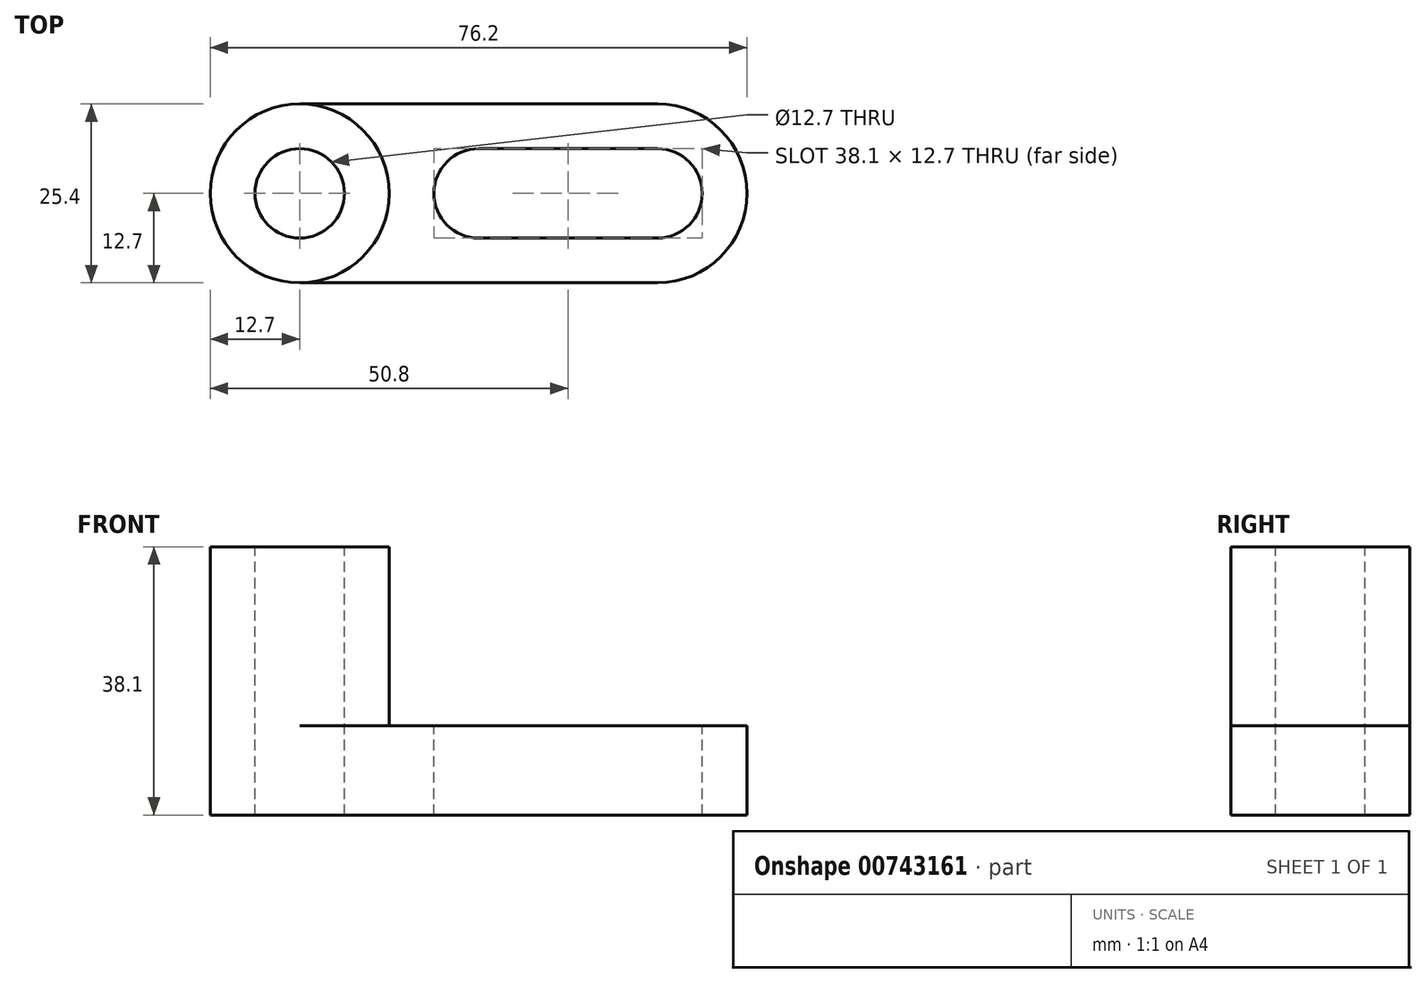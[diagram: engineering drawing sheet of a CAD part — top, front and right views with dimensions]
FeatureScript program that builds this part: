
annotation { "Feature Type Name" : "Feature", "Feature Type Description" : "" }
export const myFeature = defineFeature(function(context is Context, id is Id, definition is map)
    precondition{}
    {
        {
            var Q0;
            Q0=qCreatedBy(makeId("Top.planeOp"),FACE);
            var sketch = newSketch(context, id + "F0", { "sketchPlane" : qUnion([Q0])});
            skLineSegment(sketch, "E0.bottom", {"start": v(0, 0) * mm, "end": v(50.8, 0) * mm});
            skLineSegment(sketch, "E0.top", {"start": v(0, 25.4) * mm, "end": v(50.8, 25.4) * mm});
            skLineSegment(sketch, "E0.left", {"start": v(0, 0) * mm, "end": v(0, 25.4) * mm});
            skLineSegment(sketch, "E0.right", {"start": v(50.8, 0) * mm, "end": v(50.8, 25.4) * mm});
            skArc(sketch, "E1", {"start": v(50.8, 0) * mm, "mid": v(63.5, 12.7) * mm, "end": v(50.8, 25.4) * mm});
            skArc(sketch, "E2", {"start": v(0, 25.4) * mm, "mid": v(-12.7, 12.7) * mm, "end": v(0, 0) * mm});
            skSolve(sketch);
        }
        {
            var Q0;
            Q0=makeQuery(id+"F0.imprint","IMPRINT",FACE,{"disambiguationData":[TD([[makeQuery(id+"F0.imprint","IMPRINT",EDGE,{"derivedFrom":sQuery(id+"F0.wireOp",EDGE,"E0.left")}),1.0]])]});
            extrude(context, id + "F1", {"entities" : qUnion([Q0]), "depth" : 38.1 * mm, "offsetDistance" : 25.4 * mm});
        }
        {
            var Q0;
            Q0 = qSketchRegion(id + "F0", true);
            extrude(context, id + "F2", {"entities" : qUnion([Q0]), "operationType" : NewBodyOperationType.ADD, "depth" : 12.7 * mm, "offsetDistance" : 25.4 * mm});
        }
        {
            var Q0;
            Q0=makeQuery(id+"F2.opExtrude","CAP_FACE",FACE,{"disambiguationData":[OSD([sQuery(id+"F0.wireOp",EDGE,"E0.bottom"),sQuery(id+"F0.wireOp",EDGE,"E0.top"),sQuery(id+"F0.wireOp",EDGE,"E1"),sQuery(id+"F0.wireOp",EDGE,"E2")])],"isStart":false});
            var sketch = newSketch(context, id + "F3", { "sketchPlane" : qUnion([Q0])});
            skArc(sketch, "E3", {"start": v(0, 0) * mm, "mid": v(12.7, 12.7) * mm, "end": v(0, 25.4) * mm});
            skSolve(sketch);
        }
        {
            var Q0;
            Q0=makeQuery(id+"F3.imprint","IMPRINT",FACE,{"disambiguationData":[TD([[makeQuery(id+"F3.imprint","IMPRINT",EDGE,{"derivedFrom":sQuery(id+"F3.wireOp",EDGE,"E3")}),1.0]])]});
            extrude(context, id + "F4", {"entities" : qUnion([Q0]), "operationType" : NewBodyOperationType.ADD, "depth" : 25.4 * mm, "offsetDistance" : 25.4 * mm});
        }
        {
            var Q0;
            Q0=makeQuery(id+"F2.opExtrude","CAP_FACE",FACE,{"disambiguationData":[OSD([sQuery(id+"F0.wireOp",EDGE,"E0.bottom"),sQuery(id+"F0.wireOp",EDGE,"E0.top"),sQuery(id+"F0.wireOp",EDGE,"E1"),sQuery(id+"F0.wireOp",EDGE,"E2")])],"isStart":false});
            var sketch = newSketch(context, id + "F5", { "sketchPlane" : qUnion([Q0])});
            skLineSegment(sketch, "E4.bottom", {"start": v(25.4, 19.05) * mm, "end": v(50.8, 19.05) * mm});
            skLineSegment(sketch, "E4.top", {"start": v(25.4, 6.35) * mm, "end": v(50.8, 6.35) * mm});
            skLineSegment(sketch, "E4.left", {"start": v(25.4, 19.05) * mm, "end": v(25.4, 6.35) * mm});
            skLineSegment(sketch, "E4.right", {"start": v(50.8, 19.05) * mm, "end": v(50.8, 6.35) * mm});
            skArc(sketch, "E5", {"start": v(25.4, 19.05) * mm, "mid": v(19.05, 12.7) * mm, "end": v(25.4, 6.35) * mm});
            skArc(sketch, "E6", {"start": v(50.8, 6.35) * mm, "mid": v(57.15, 12.7) * mm, "end": v(50.8, 19.05) * mm});
            skSolve(sketch);
        }
        {
            var Q0;
            Q0=makeQuery(id+"F5.imprint","IMPRINT",FACE,{"disambiguationData":[TD([[makeQuery(id+"F5.imprint","IMPRINT",EDGE,{"derivedFrom":sQuery(id+"F5.wireOp",EDGE,"E4.left")}),-1.0]])]});
            var Q1;
            Q1=makeQuery(id+"F5.imprint","IMPRINT",FACE,{"disambiguationData":[TD([[makeQuery(id+"F5.imprint","IMPRINT",EDGE,{"derivedFrom":sQuery(id+"F5.wireOp",EDGE,"E4.bottom")}),-1.0]])]});
            var Q2;
            Q2=makeQuery(id+"F5.imprint","IMPRINT",FACE,{"disambiguationData":[TD([[makeQuery(id+"F5.imprint","IMPRINT",EDGE,{"derivedFrom":sQuery(id+"F5.wireOp",EDGE,"E4.right")}),1.0]])]});
            extrude(context, id + "F6", {"entities" : qUnion([Q0, Q1, Q2]), "operationType" : NewBodyOperationType.REMOVE, "oppositeDirection" : true, "depth" : 25.4 * mm, "offsetDistance" : 25.4 * mm});
        }
        {
            var Q0;
            {var subQ0=sQuery(id+"F0.wireOp",EDGE,"E2");var subQ1=sQuery(id+"F0.wireOp",EDGE,"E0.left");Q0=makeQuery(id+"F4.boolean.opBoolean","MERGE",FACE,{"derivedFrom":[makeQuery(id+"F1.opExtrude","CAP_FACE",FACE,{"disambiguationData":[OSD([subQ1,subQ0])],"isStart":false}),makeQuery(id+"F4.opExtrude","CAP_FACE",FACE,{"disambiguationData":[OSD([sQuery(id+"F0.wireOp",EDGE,"E0.bottom"),sQuery(id+"F0.wireOp",EDGE,"E0.top"),subQ1,sQuery(id+"F0.wireOp",EDGE,"E1"),subQ0,sQuery(id+"F3.wireOp",EDGE,"E3")])],"isStart":false})]});}
            var sketch = newSketch(context, id + "F7", { "sketchPlane" : qUnion([Q0])});
            skCircle(sketch, "E7", {"center": v(0, 12.7) * mm, "radius": 6.35 * mm});
            skSolve(sketch);
        }
        {
            var Q0;
            Q0=makeQuery(id+"F7.imprint","IMPRINT",FACE,{"disambiguationData":[TD([[makeQuery(id+"F7.imprint","IMPRINT",EDGE,{"derivedFrom":sQuery(id+"F7.wireOp",EDGE,"E7")}),1.0]])]});
            extrude(context, id + "F8", {"entities" : qUnion([Q0]), "operationType" : NewBodyOperationType.REMOVE, "oppositeDirection" : true, "depth" : 38.1 * mm, "offsetDistance" : 25.4 * mm});
        }
    });
